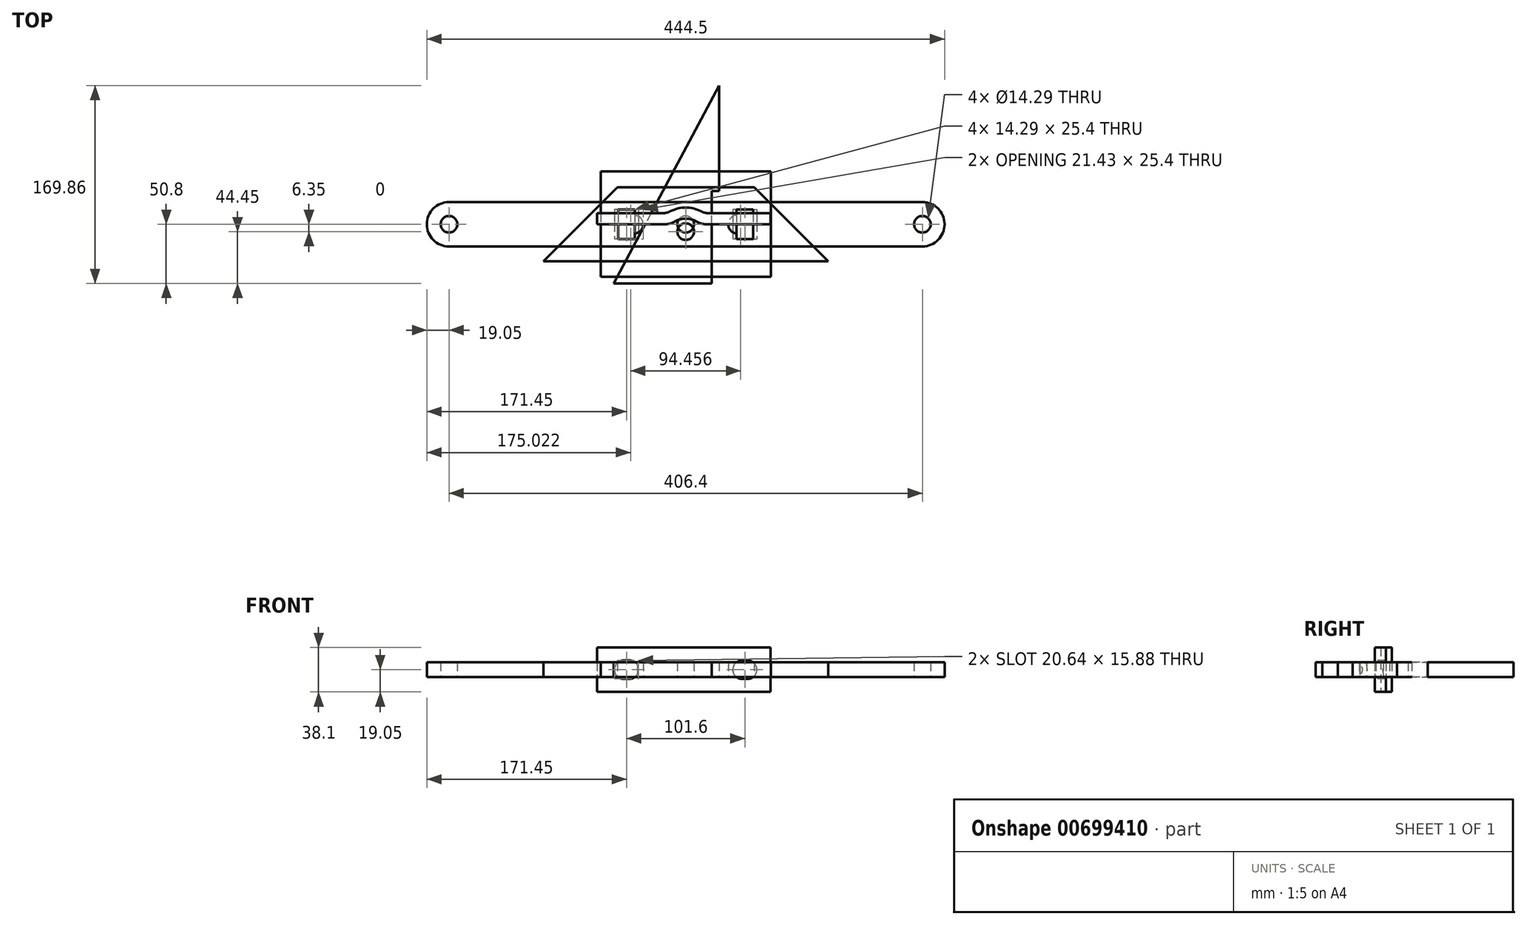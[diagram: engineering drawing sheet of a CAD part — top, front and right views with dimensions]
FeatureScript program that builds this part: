
annotation { "Feature Type Name" : "Feature", "Feature Type Description" : "" }
export const myFeature = defineFeature(function(context is Context, id is Id, definition is map)
    precondition{}
    {
        {
            var Q0;
            Q0=qCreatedBy(makeId("Top.planeOp"),FACE);
            var sketch = newSketch(context, id + "F0", { "sketchPlane" : qUnion([Q0])});
            skLineSegment(sketch, "E0.bottom", {"start": v(-73.02, 45.24) * mm, "end": v(73.03, 45.24) * mm});
            skLineSegment(sketch, "E0.top", {"start": v(-73.02, -45.24) * mm, "end": v(73.03, -45.24) * mm});
            skLineSegment(sketch, "E0.left", {"start": v(-73.02, 45.24) * mm, "end": v(-73.02, -45.24) * mm});
            skLineSegment(sketch, "E0.right", {"start": v(73.03, 45.24) * mm, "end": v(73.03, -45.24) * mm});
            skCircle(sketch, "E1", {"center": v(-44.45, 0) * mm, "radius": 7.94 * mm});
            skCircle(sketch, "E2.MirrorC", {"center": v(44.45, 0) * mm, "radius": 7.94 * mm});
            skSolve(sketch);
        }
        {
            var Q0;
            Q0 = qSketchRegion(id + "F0", true);
            extrude(context, id + "F1", {"entities" : qUnion([Q0]), "endBound" : BoundingType.SYMMETRIC, "depth" : 12.7 * mm, "offsetDistance" : 25.4 * mm});
        }
        {
            var Q0;
            Q0=qCreatedBy(makeId("Top.planeOp"),FACE);
            var sketch = newSketch(context, id + "F2", { "sketchPlane" : qUnion([Q0])});
            skLineSegment(sketch, "E3", {"start": v(-122.24, -31.75) * mm, "end": v(122.24, -31.75) * mm});
            skLineSegment(sketch, "E4", {"start": v(122.24, -31.75) * mm, "end": v(58.74, 31.75) * mm});
            skLineSegment(sketch, "E5", {"start": v(58.74, 31.75) * mm, "end": v(-58.74, 31.75) * mm});
            skLineSegment(sketch, "E6", {"start": v(-58.74, 31.75) * mm, "end": v(-122.24, -31.75) * mm});
            skCircle(sketch, "E7", {"center": v(0, -6.35) * mm, "radius": 7.14 * mm});
            skSolve(sketch);
        }
        {
            var Q0;
            Q0 = qSketchRegion(id + "F2", true);
            extrude(context, id + "F3", {"entities" : qUnion([Q0]), "endBound" : BoundingType.SYMMETRIC, "depth" : 12.7 * mm, "offsetDistance" : 25.4 * mm});
        }
        {
            var Q0;
            Q0=qCreatedBy(makeId("Top.planeOp"),FACE);
            var sketch = newSketch(context, id + "F4", { "sketchPlane" : qUnion([Q0])});
            skLineSegment(sketch, "E8", {"start": v(-61.91, -50.8) * mm, "end": v(22.23, -50.8) * mm});
            skLineSegment(sketch, "E9", {"start": v(22.23, -50.8) * mm, "end": v(22.23, 28.57) * mm});
            skLineSegment(sketch, "E10", {"start": v(22.23, 28.57) * mm, "end": v(28.58, 28.57) * mm});
            skLineSegment(sketch, "E11", {"start": v(28.58, 28.57) * mm, "end": v(28.58, 119.06) * mm});
            skLineSegment(sketch, "E12", {"start": v(28.57, 119.06) * mm, "end": v(-61.91, -50.8) * mm});
            skCircle(sketch, "E13", {"center": v(0, 0) * mm, "radius": 7.14 * mm});
            skSolve(sketch);
        }
        {
            var Q0;
            Q0 = qSketchRegion(id + "F4", true);
            extrude(context, id + "F5", {"entities" : qUnion([Q0]), "endBound" : BoundingType.SYMMETRIC, "depth" : 12.7 * mm, "offsetDistance" : 25.4 * mm});
        }
        {
            var Q0;
            Q0=qCreatedBy(makeId("Top.planeOp"),FACE);
            var sketch = newSketch(context, id + "F6", { "sketchPlane" : qUnion([Q0])});
            skLineSegment(sketch, "E14.bottom", {"start": v(-203.2, 19.05) * mm, "end": v(203.2, 19.05) * mm});
            skLineSegment(sketch, "E14.top", {"start": v(-203.2, -19.05) * mm, "end": v(203.2, -19.05) * mm});
            skArc(sketch, "E15", {"start": v(-203.2, 19.05) * mm, "mid": v(-222.25, 0) * mm, "end": v(-203.2, -19.05) * mm});
            skCircle(sketch, "E16", {"center": v(-203.2, 0) * mm, "radius": 7.14 * mm});
            skPoint(sketch, "E17.center.orphan", {"position": v(-66.89, 0) * mm});
            skArc(sketch, "E18.MirrorCS", {"start": v(203.2, 19.05) * mm, "mid": v(222.25, 0) * mm, "end": v(203.2, -19.05) * mm});
            skCircle(sketch, "E19.MirrorC", {"center": v(203.2, 0) * mm, "radius": 7.14 * mm});
            skSolve(sketch);
        }
        {
            var Q0;
            Q0 = qSketchRegion(id + "F6", true);
            extrude(context, id + "F7", {"entities" : qUnion([Q0]), "endBound" : BoundingType.SYMMETRIC, "depth" : 12.7 * mm, "offsetDistance" : 25.4 * mm});
        }
        {
            var Q0;
            Q0=qCreatedBy(makeId("Top.planeOp"),FACE);
            var sketch = newSketch(context, id + "F8", { "sketchPlane" : qUnion([Q0])});
            skLineSegment(sketch, "E20.bottom", {"start": v(-76.2, 9.51) * mm, "end": v(-19.35, 9.51) * mm});
            skLineSegment(sketch, "E20.top", {"start": v(-76.2, -0.01) * mm, "end": v(-17.7, -0.01) * mm});
            skLineSegment(sketch, "E20.left", {"start": v(-76.2, 9.51) * mm, "end": v(-76.2, -0.01) * mm});
            skLineSegment(sketch, "E20.right", {"start": v(72.76, 9.51) * mm, "end": v(72.76, -0.01) * mm});
            skArc(sketch, "E21", {"start": v(13.4, 11) * mm, "mid": v(0, 14.33) * mm, "end": v(-13.4, 11) * mm});
            skArc(sketch, "E22", {"start": v(9.65, 2.18) * mm, "mid": v(0, 4.8) * mm, "end": v(-9.65, 2.18) * mm});
            skLineSegment(sketch, "E23.trimOffspring", {"start": v(17.7, -0.01) * mm, "end": v(72.76, -0.01) * mm});
            skLineSegment(sketch, "E24.trimOffspring", {"start": v(19.35, 9.51) * mm, "end": v(72.76, 9.51) * mm});
            skPoint(sketch, "E25.visualSharp", {"position": v(-15.88, 9.51) * mm});
            skArc(sketch, "E25.filletArc", {"start": v(-19.35, 9.51) * mm, "mid": v(-16.28, 9.9) * mm, "end": v(-13.4, 11) * mm});
            skPoint(sketch, "E26.visualSharp", {"position": v(15.88, 9.51) * mm});
            skArc(sketch, "E26.filletArc", {"start": v(13.4, 11) * mm, "mid": v(16.28, 9.9) * mm, "end": v(19.35, 9.51) * mm});
            skPoint(sketch, "E27.visualSharp", {"position": v(-12.66, -0.01) * mm});
            skArc(sketch, "E27.filletArc", {"start": v(-17.7, -0.01) * mm, "mid": v(-13.53, 0.55) * mm, "end": v(-9.65, 2.18) * mm});
            skPoint(sketch, "E28.visualSharp", {"position": v(12.66, -0.01) * mm});
            skArc(sketch, "E28.filletArc", {"start": v(9.65, 2.18) * mm, "mid": v(13.53, 0.55) * mm, "end": v(17.7, -0.01) * mm});
            skSolve(sketch);
        }
        {
            var Q0;
            Q0 = qSketchRegion(id + "F8", true);
            extrude(context, id + "F9", {"entities" : qUnion([Q0]), "endBound" : BoundingType.SYMMETRIC, "depth" : 38.1 * mm, "offsetDistance" : 25.4 * mm});
        }
        {
            var Q0;
            Q0=qCreatedBy(makeId("Front.planeOp"),FACE);
            var sketch = newSketch(context, id + "F10", { "sketchPlane" : qUnion([Q0])});
            skArc(sketch, "E29", {"start": v(-53.18, 7.94) * mm, "mid": v(-61.12, 0) * mm, "end": v(-53.18, -7.94) * mm});
            skArc(sketch, "E30", {"start": v(-48.42, -7.94) * mm, "mid": v(-40.48, 0) * mm, "end": v(-48.42, 7.94) * mm});
            skLineSegment(sketch, "E31", {"start": v(-53.18, 7.94) * mm, "end": v(-48.42, 7.94) * mm});
            skLineSegment(sketch, "E32", {"start": v(-53.18, -7.94) * mm, "end": v(-48.42, -7.94) * mm});
            skArc(sketch, "E33.MirrorCS", {"start": v(48.42, -7.94) * mm, "mid": v(40.48, 0) * mm, "end": v(48.42, 7.94) * mm});
            skLineSegment(sketch, "E34.MirrorCS", {"start": v(53.18, 7.94) * mm, "end": v(48.42, 7.94) * mm});
            skArc(sketch, "E35.MirrorCS", {"start": v(53.18, 7.94) * mm, "mid": v(61.12, 0) * mm, "end": v(53.18, -7.94) * mm});
            skLineSegment(sketch, "E36.MirrorCS", {"start": v(53.18, -7.94) * mm, "end": v(48.42, -7.94) * mm});
            skSolve(sketch);
        }
        {
            var Q0;
            Q0 = qSketchRegion(id + "F10", true);
            extrude(context, id + "F11", {"entities" : qUnion([Q0]), "operationType" : NewBodyOperationType.REMOVE, "endBound" : BoundingType.SYMMETRIC, "oppositeDirection" : true, "depth" : 25.4 * mm, "offsetDistance" : 25.4 * mm});
        }
    });
